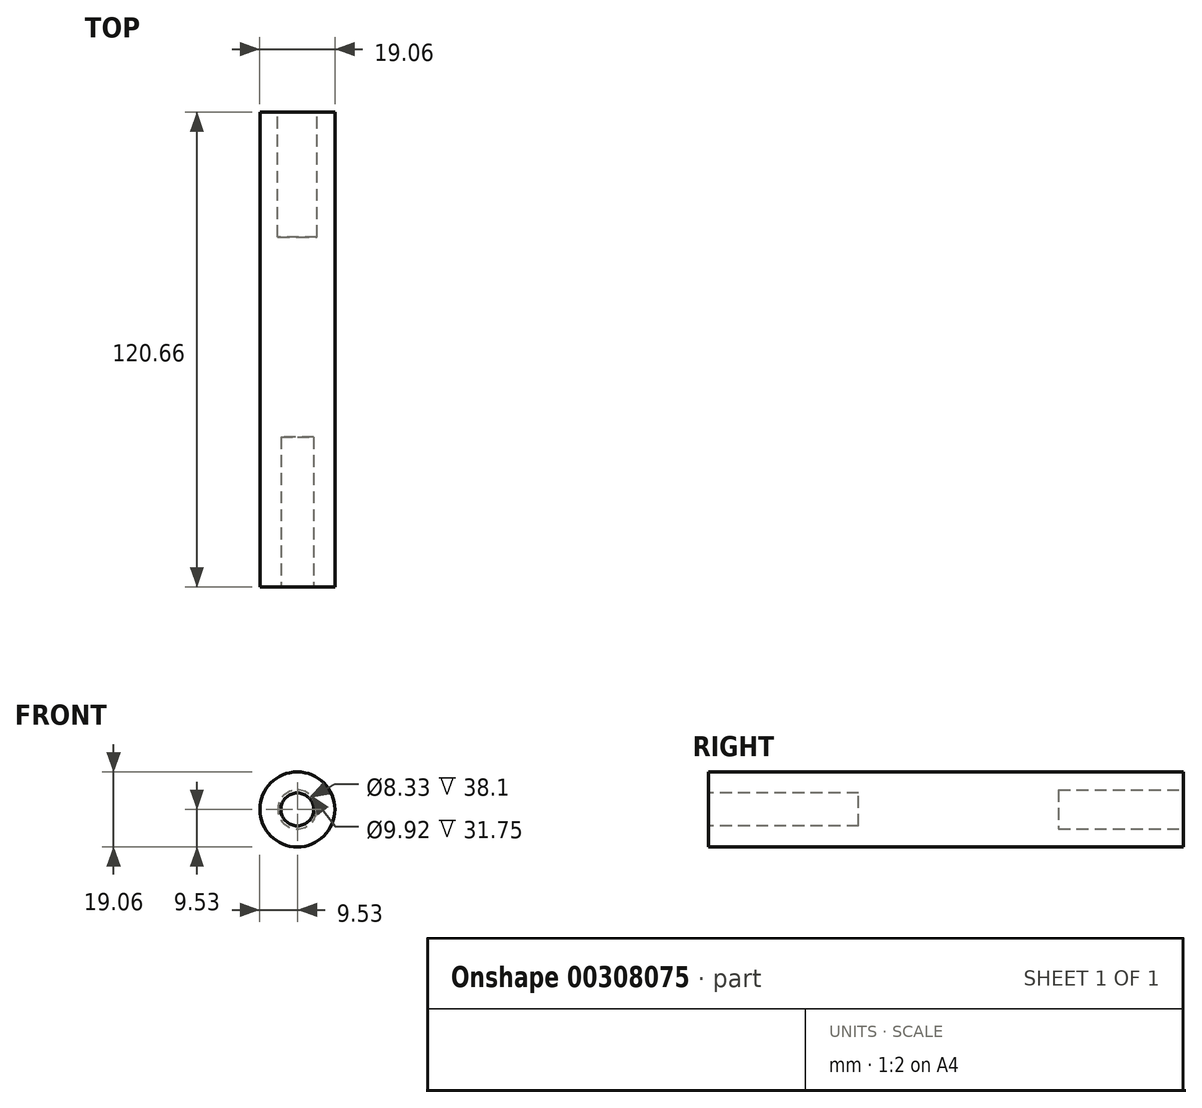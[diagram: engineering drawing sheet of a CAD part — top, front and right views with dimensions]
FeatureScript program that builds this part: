
annotation { "Feature Type Name" : "Feature", "Feature Type Description" : "" }
export const myFeature = defineFeature(function(context is Context, id is Id, definition is map)
    precondition{}
    {
        {
            var Q0;
            Q0=qCreatedBy(makeId("Front.planeOp"),FACE);
            var sketch = newSketch(context, id + "F0", { "sketchPlane" : qUnion([Q0])});
            skCircle(sketch, "E0", {"center": v(0, 0) * mm, "radius": 9.53 * mm});
            skSolve(sketch);
        }
        {
            var Q0;
            Q0 = qSketchRegion(id + "F0", true);
            extrude(context, id + "F1", {"entities" : qUnion([Q0]), "endBound" : BoundingType.SYMMETRIC, "depth" : 120.65 * mm, "offsetDistance" : 25.4 * mm});
        }
        {
            var Q0;
            Q0=makeQuery(id+"F1.opExtrude","CAP_FACE",FACE,{"disambiguationData":[OSD([sQuery(id+"F0.wireOp",EDGE,"E0")])],"isStart":false});
            var sketch = newSketch(context, id + "F2", { "sketchPlane" : qUnion([Q0])});
            skCircle(sketch, "E1.0", {"center": v(0, 0) * mm, "radius": 9.53 * mm});
            skCircle(sketch, "E2", {"center": v(0, 0) * mm, "radius": 4.17 * mm});
            skSolve(sketch);
        }
        {
            var Q0;
            Q0=makeQuery(id+"F2.imprint","IMPRINT",FACE,{"disambiguationData":[TD([[makeQuery(id+"F2.imprint","IMPRINT",EDGE,{"derivedFrom":sQuery(id+"F2.wireOp",EDGE,"E2")}),1.0]])]});
            extrude(context, id + "F3", {"entities" : qUnion([Q0]), "operationType" : NewBodyOperationType.REMOVE, "oppositeDirection" : true, "depth" : 38.1 * mm, "offsetDistance" : 25.4 * mm});
        }
        {
            var Q0;
            Q0=makeQuery(id+"F1.opExtrude","CAP_FACE",FACE,{"disambiguationData":[OSD([sQuery(id+"F0.wireOp",EDGE,"E0")])],"isStart":true});
            var sketch = newSketch(context, id + "F4", { "sketchPlane" : qUnion([Q0])});
            skCircle(sketch, "E3.0", {"center": v(0, 0) * mm, "radius": 9.53 * mm});
            skCircle(sketch, "E4", {"center": v(0, 0) * mm, "radius": 4.96 * mm});
            skSolve(sketch);
        }
        {
            var Q0;
            Q0=makeQuery(id+"F4.imprint","IMPRINT",FACE,{"disambiguationData":[TD([[makeQuery(id+"F4.imprint","IMPRINT",EDGE,{"derivedFrom":sQuery(id+"F4.wireOp",EDGE,"E4")}),1.0]])]});
            extrude(context, id + "F5", {"entities" : qUnion([Q0]), "operationType" : NewBodyOperationType.REMOVE, "oppositeDirection" : true, "depth" : 31.75 * mm, "offsetDistance" : 25.4 * mm});
        }
    });
